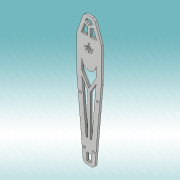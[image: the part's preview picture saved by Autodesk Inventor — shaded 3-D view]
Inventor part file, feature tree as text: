
AUTODESK INVENTOR PART (.ipt)
format: ipt  version: 2019 (Build 230136000, 136)  size: 214,528 bytes
history: native  units: mm
features: extrude x2
ambient origin geometry x8: Origin, YZ Plane, XZ Plane, XY Plane, X Axis, Y Axis, Z Axis, Center Point
bodies: Solid1 (feature_tree)
feature tree (2):
  extrude  "Extrusion1"  Depth=7.0mm
  extrude  "Extrusion2"  Depth=6.0mm
